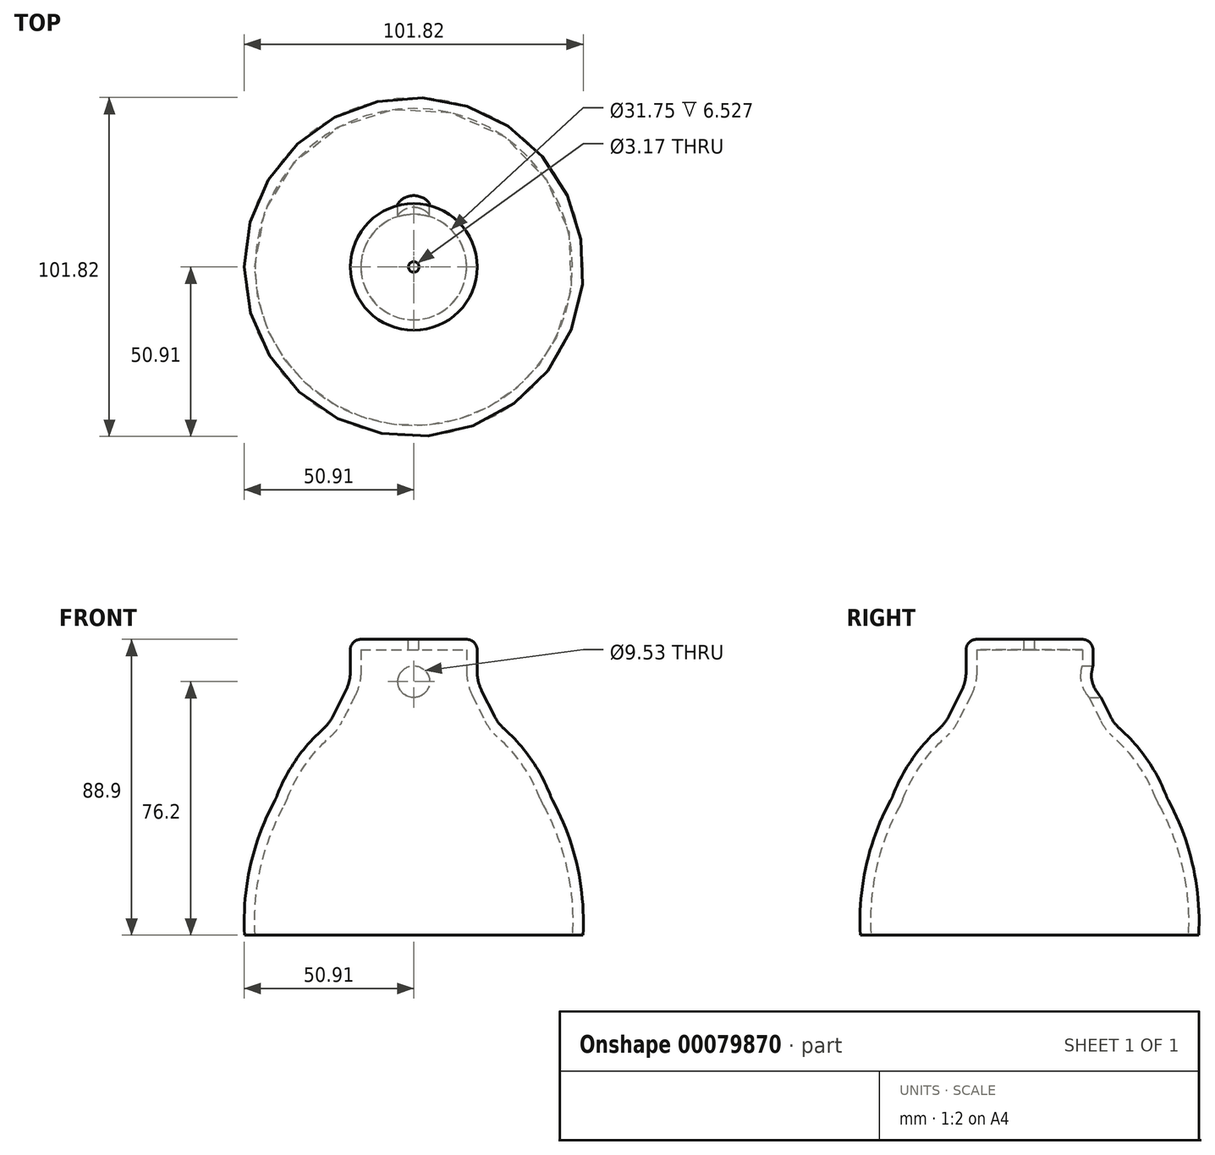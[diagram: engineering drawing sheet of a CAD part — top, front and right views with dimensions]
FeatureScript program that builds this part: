
annotation { "Feature Type Name" : "Feature", "Feature Type Description" : "" }
export const myFeature = defineFeature(function(context is Context, id is Id, definition is map)
    precondition{}
    {
        {
            var Q0;
            Q0=qCreatedBy(makeId("Front.planeOp"),FACE);
            var sketch = newSketch(context, id + "F0", { "sketchPlane" : qUnion([Q0])});
            skLineSegment(sketch, "E0", {"start": v(0, 0) * mm, "end": v(50.8, 0) * mm});
            skLineSegment(sketch, "E1", {"start": v(0, 0) * mm, "end": v(0, 88.9) * mm});
            skLineSegment(sketch, "E2", {"start": v(0, 88.9) * mm, "end": v(19.05, 88.9) * mm});
            skLineSegment(sketch, "E3", {"start": v(19.05, 63.5) * mm, "end": v(25.4, 63.5) * mm, "construction": true});
            skLineSegment(sketch, "E4", {"start": v(19.05, 88.9) * mm, "end": v(19.05, 76.2) * mm});
            skLineSegment(sketch, "E5", {"start": v(19.05, 76.2) * mm, "end": v(25.4, 63.5) * mm});
            skLineSegment(sketch, "E6", {"start": v(25.4, 63.5) * mm, "end": v(25.4, 41.27) * mm, "construction": true});
            skLineSegment(sketch, "E7", {"start": v(25.4, 41.27) * mm, "end": v(41.28, 41.27) * mm, "construction": true});
            skArc(sketch, "E8", {"start": v(41.27, 41.27) * mm, "mid": v(34.86, 53.47) * mm, "end": v(25.4, 63.5) * mm});
            skArc(sketch, "E9", {"start": v(50.8, 0) * mm, "mid": v(48.96, 21.31) * mm, "end": v(41.28, 41.28) * mm});
            skSolve(sketch);
        }
        {
            var Q0;
            Q0=qCreatedBy(makeId("Front.planeOp"),FACE);
            var sketch = newSketch(context, id + "F1", { "sketchPlane" : qUnion([Q0])});
            skLineSegment(sketch, "E10", {"start": v(0, -23.27) * mm, "end": v(0, 144.8) * mm});
            skSolve(sketch);
        }
        {
            var Q0;
            Q0=makeQuery(id+"F0.imprint","IMPRINT",FACE,{"disambiguationData":[TD([[makeQuery(id+"F0.imprint","IMPRINT",EDGE,{"derivedFrom":sQuery(id+"F0.wireOp",EDGE,"E0")}),1.0]])]});
            var Q1;
            Q1=sQuery(id+"F1.wireOp",EDGE,"E10");
            revolve(context, id + "F2", {"entities" : qUnion([Q0]), "axis" : qUnion([Q1]), "revolveType" : RevolveType.FULL});
        }
        {
            var Q0;
            Q0=makeQuery(id+"F2.opRevolve","SWEPT_EDGE",EDGE,{"disambiguationData":[OSD([sQuery(id+"F0.wireOp",EDGE,"E4"),sQuery(id+"F0.wireOp",EDGE,"E5")])]});
            var Q1;
            Q1=makeQuery(id+"F2.opRevolve","SWEPT_EDGE",EDGE,{"disambiguationData":[OSD([sQuery(id+"F0.wireOp",EDGE,"E5"),sQuery(id+"F0.wireOp",EDGE,"E8")])]});
            var Q2;
            Q2=makeQuery(id+"F2.opRevolve","SWEPT_EDGE",EDGE,{"disambiguationData":[OSD([sQuery(id+"F0.wireOp",EDGE,"E8"),sQuery(id+"F0.wireOp",EDGE,"E9")])]});
            fillet(context, id + "F3", {"entities" : qUnion([Q0, Q1, Q2]), "radius" : 12.7 * mm, "tangentPropagation" : true, "allowEdgeOverflow" : false});
        }
        {
            var Q0;
            Q0=makeQuery(id+"F2.opRevolve","SWEPT_EDGE",EDGE,{"disambiguationData":[OSD([sQuery(id+"F0.wireOp",EDGE,"E2"),sQuery(id+"F0.wireOp",EDGE,"E4")])]});
            fillet(context, id + "F4", {"entities" : qUnion([Q0]), "radius" : 3.17 * mm, "tangentPropagation" : true, "allowEdgeOverflow" : false});
        }
        {
            var Q0;
            Q0=makeQuery(id+"F2.opRevolve","SWEPT_FACE",FACE,{"disambiguationData":[OSD([sQuery(id+"F0.wireOp",EDGE,"E0")])]});
            shell(context, id + "F5", {"entities" : qUnion([Q0]), "thickness" : 3.17 * mm});
        }
        {
            var Q0;
            Q0=makeQuery(id+"F2.opRevolve","SWEPT_FACE",FACE,{"disambiguationData":[OSD([sQuery(id+"F0.wireOp",EDGE,"E2")])]});
            var sketch = newSketch(context, id + "F6", { "sketchPlane" : qUnion([Q0])});
            skPoint(sketch, "E11", {"position": v(0, 0) * mm});
            skSolve(sketch);
        }
        {
            var Q0;
            Q0=sQuery(id+"F6.wireOp",VERTEX,"E11");
            var Q1;
            Q1=makeQuery(id+"F2.opRevolve","SWEPT_BODY",BODY,{"disambiguationData":[OSD([sQuery(id+"F0.wireOp",EDGE,"E0"),sQuery(id+"F0.wireOp",EDGE,"E1"),sQuery(id+"F0.wireOp",EDGE,"E2"),sQuery(id+"F0.wireOp",EDGE,"E4"),sQuery(id+"F0.wireOp",EDGE,"E5"),sQuery(id+"F0.wireOp",EDGE,"E8"),sQuery(id+"F0.wireOp",EDGE,"E9")])]});
            hole(context, id + "F7", {"style" : HoleStyle.SIMPLE, "endStyle" : HoleEndStyle.THROUGH, "holeDiameter" : 3.17 * mm, "locations" : qUnion([Q0]), "scope" : qUnion([Q1]), "isTappedThrough" : true});
        }
        {
            var Q0;
            Q0=qCreatedBy(makeId("Front.planeOp"),FACE);
            cPlane(context, id + "F8", {"entities" : qUnion([Q0]), "cplaneType" : CPlaneType.OFFSET, "offset" : 50.8 * mm, "oppositeDirection" : true, "width" : 152.4 * mm, "height" : 152.4 * mm});
        }
        {
            var Q0;
            Q0=qCreatedBy(id+"F8.planeOp",FACE);
            var sketch = newSketch(context, id + "F9", { "sketchPlane" : qUnion([Q0])});
            skPoint(sketch, "E12", {"position": v(0, 76.2) * mm});
            skCircle(sketch, "E13", {"center": v(0, 76.2) * mm, "radius": 4.76 * mm});
            skSolve(sketch);
        }
        {
            var Q0;
            Q0=makeQuery(id+"F9.imprint","IMPRINT",FACE,{"disambiguationData":[TD([[makeQuery(id+"F9.imprint","IMPRINT",EDGE,{"derivedFrom":sQuery(id+"F9.wireOp",EDGE,"E13")}),1.0]])]});
            extrude(context, id + "F10", {"entities" : qUnion([Q0]), "operationType" : NewBodyOperationType.REMOVE, "depth" : 50.8 * mm});
        }
    });
